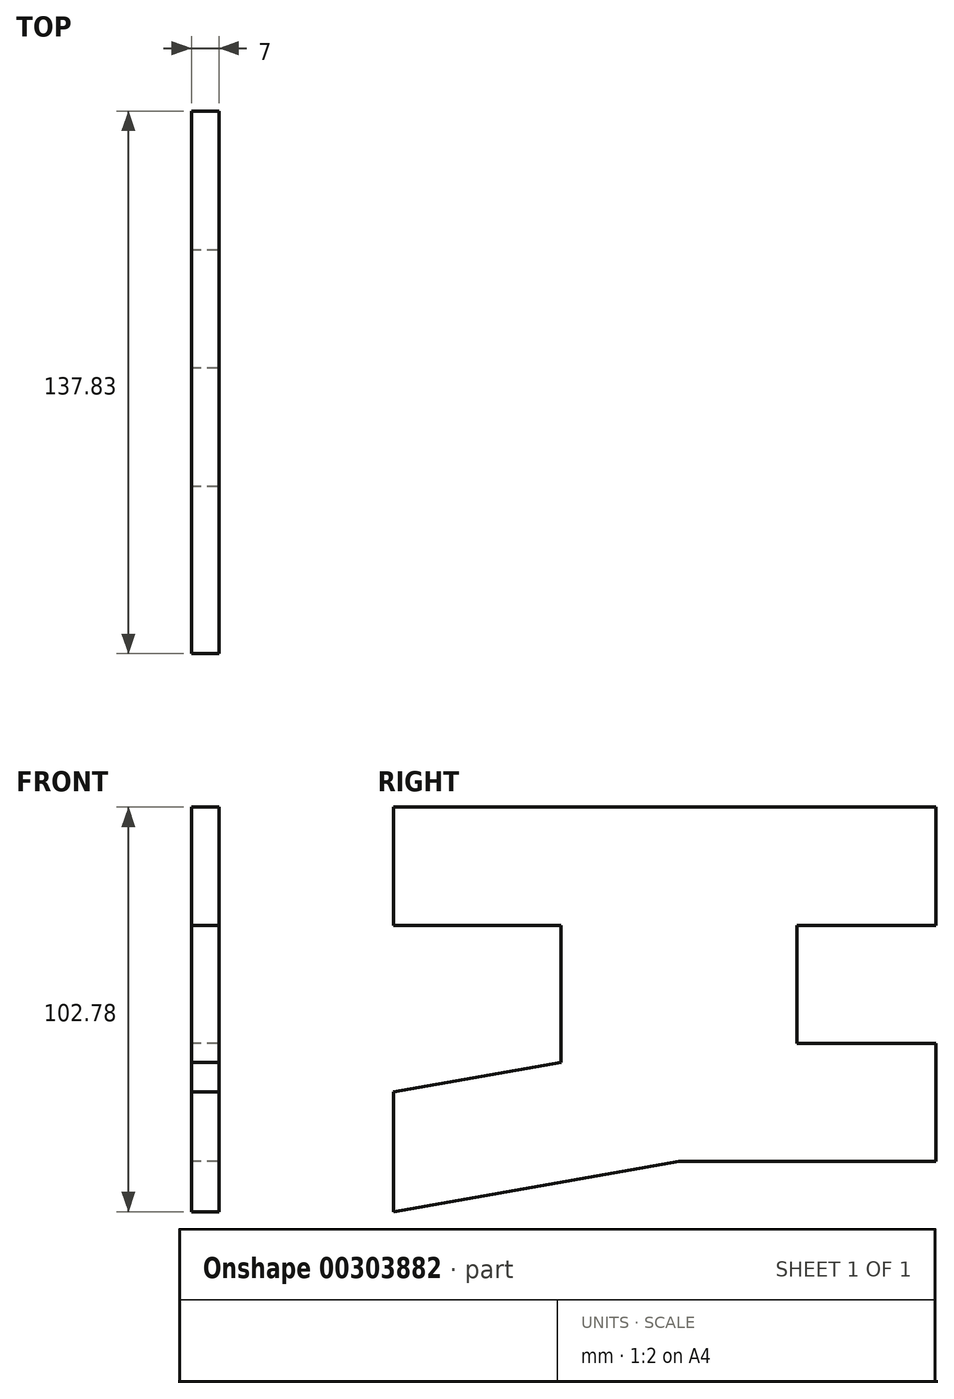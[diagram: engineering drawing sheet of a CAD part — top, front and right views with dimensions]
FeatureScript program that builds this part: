
annotation { "Feature Type Name" : "Feature", "Feature Type Description" : "" }
export const myFeature = defineFeature(function(context is Context, id is Id, definition is map)
    precondition{}
    {
        {
            var Q0;
            Q0=qCreatedBy(makeId("Right.planeOp"),FACE);
            var sketch = newSketch(context, id + "F0", { "sketchPlane" : qUnion([Q0])});
            skLineSegment(sketch, "E0.bottom", {"start": v(-123.23, 82) * mm, "end": v(-50.73, 82) * mm});
            skLineSegment(sketch, "E0.top", {"start": v(-123.23, -20.78) * mm, "end": v(-50.73, -8) * mm});
            skLineSegment(sketch, "E1.2", {"start": v(-80.73, 52) * mm, "end": v(-80.73, 17.18) * mm});
            skLineSegment(sketch, "E2.trimOffspring", {"start": v(-123.23, 52) * mm, "end": v(-80.73, 52) * mm});
            skLineSegment(sketch, "E3.trimOffspring", {"start": v(-123.23, 9.68) * mm, "end": v(-80.73, 17.18) * mm});
            skLineSegment(sketch, "E4.bottom", {"start": v(-50.73, 82) * mm, "end": v(14.6, 82) * mm});
            skLineSegment(sketch, "E4.top", {"start": v(-50.73, -8) * mm, "end": v(14.6, -8) * mm});
            skLineSegment(sketch, "E5.0", {"start": v(-20.73, 52) * mm, "end": v(-20.73, 22) * mm});
            skLineSegment(sketch, "E5.1", {"start": v(-20.73, 52) * mm, "end": v(14.6, 52) * mm});
            skLineSegment(sketch, "E5.3", {"start": v(-20.73, 22) * mm, "end": v(14.6, 22) * mm});
            skLineSegment(sketch, "E6", {"start": v(-123.23, 82) * mm, "end": v(-123.23, 52) * mm});
            skLineSegment(sketch, "E7", {"start": v(14.6, 52) * mm, "end": v(14.6, 82) * mm});
            skLineSegment(sketch, "E8", {"start": v(14.6, 22) * mm, "end": v(14.6, -8) * mm});
            skLineSegment(sketch, "E9", {"start": v(14.6, -8) * mm, "end": v(-50.73, -8) * mm});
            skLineSegment(sketch, "E10", {"start": v(-123.23, 9.68) * mm, "end": v(-123.23, -20.78) * mm});
            skSolve(sketch);
        }
        {
            var Q0;
            Q0=makeQuery(id+"F0.imprint","IMPRINT",FACE,{"disambiguationData":[TD([[makeQuery(id+"F0.imprint","IMPRINT",EDGE,{"derivedFrom":sQuery(id+"F0.wireOp",EDGE,"E0.bottom")}),-1.0]])]});
            extrude(context, id + "F1", {"entities" : qUnion([Q0]), "depth" : 7 * mm});
        }
    });
